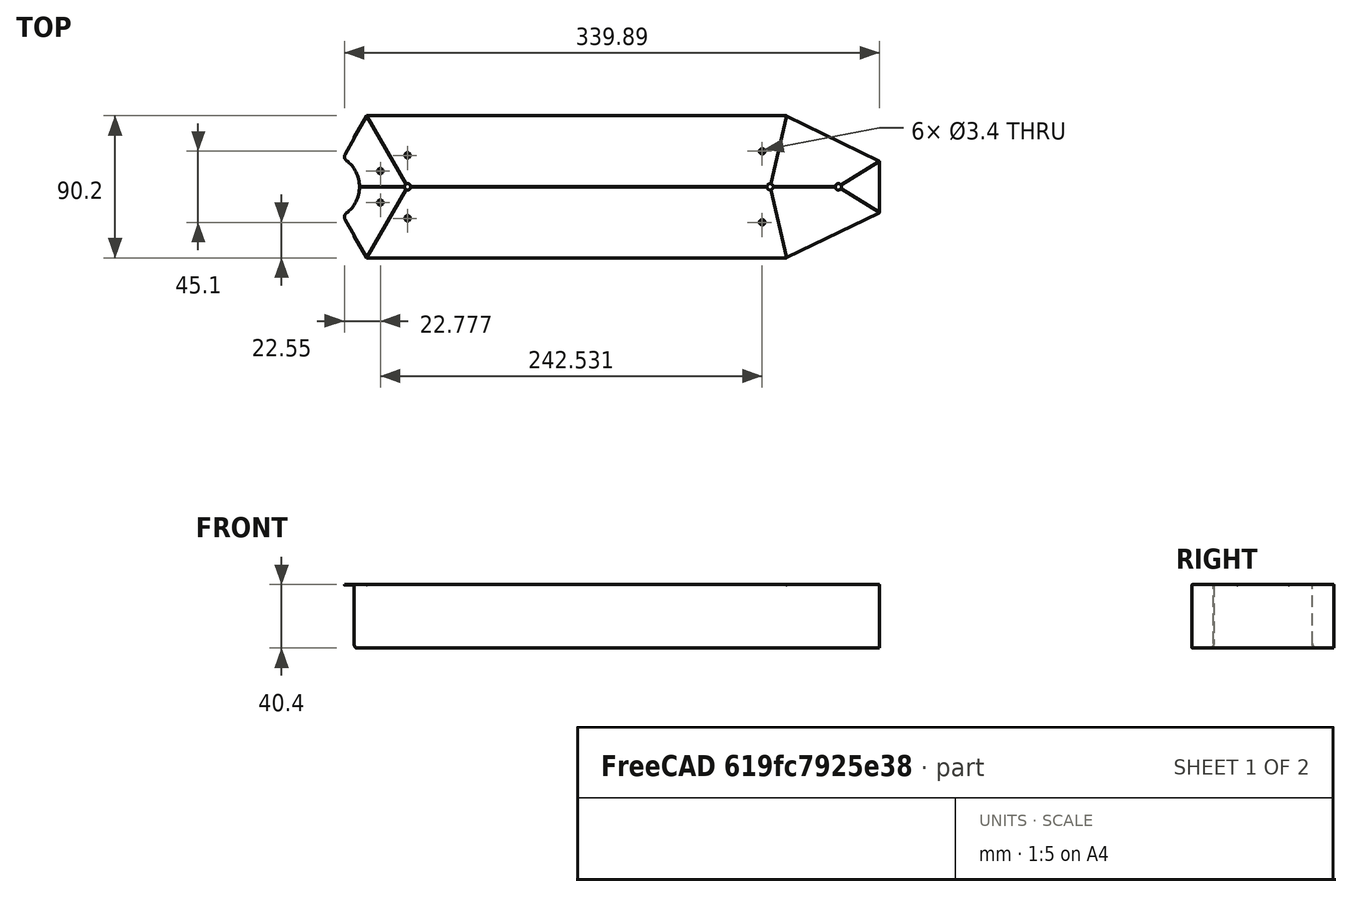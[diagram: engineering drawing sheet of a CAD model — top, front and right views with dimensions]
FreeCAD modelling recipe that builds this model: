
FCSTD DOCUMENT  (FreeCAD 1.1R38827 (Git))
Label: composit_stand3_dropper_fix_cap_outer_main
License: All rights reserved
LicenseURL: http://en.wikipedia.org/wiki/All_rights_reserved
objects: Part::FeaturePython×8, Sketcher::SketchObject×4, Part::Feature×1, PartDesign::SubShapeBinder×1, Part::Offset2D×1, Spreadsheet::Sheet×1
note: 19 computed .brp shape members not serialized (recipe doc carries the construction recipe); baked Part::Feature solids carry a one-line shape summary decoded from their .brp
EXTERNAL_REF file=composit_stand3_dropper_fix_main.FCStd obj=Sketch

FEATURE [Part::Feature] Body168  label="cap_outer_material_0.30ansi002"
  Placement = pos=(0,0,0) rot=(0,0,-1;1.5708rad)
  shape: bbox 339.9 x 90.2 x 40.4 mm, 133 faces (baked)
FEATURE [PartDesign::SubShapeBinder] Binder
  BindCopyOnChange = 0
  BindMode = 0
  ClaimChildren = false
  Fuse = false
  MakeFace = true
  OffsetFill = false
  OffsetIntersection = false
  OffsetJoinType = 0
  OffsetOpenResult = false
  PartialLoad = false
  Relative = true
  Support = -> [<external composit_stand3_dropper_fix_main.FCStd>#Sketch]
  _Version = 2
FEATURE [Sketcher::SketchObject] Sketch  label="main_sketch"
  ArcFitTolerance = 0
  ExternalGeometry = -> [Binder]
  FullyConstrained = true
  MakeInternals = false
  sketch-geometry (10):
    g0: LineSegment StartX=351.872 StartY=0 StartZ=0 EndX=351.872 EndY=16.378 EndZ=0
    g1: LineSegment StartX=351.872 StartY=16.378 StartZ=0 EndX=292.736 EndY=45.1 EndZ=0
    g2: LineSegment StartX=292.736 StartY=45.1 StartZ=0 EndX=26.0385 EndY=45.1 EndZ=0
    g3: LineSegment StartX=26.0385 StartY=45.1 StartZ=0 EndX=0.23094 EndY=0.4 EndZ=0
    g4: LineSegment [constr] StartX=292.046 StartY=45.1 StartZ=0 EndX=292.046 EndY=42.1 EndZ=0
    g5: LineSegment [constr] StartX=292.046 StartY=42.1 StartZ=0 EndX=293.356 EndY=44.7985 EndZ=0
    g6: LineSegment [constr] StartX=351.872 StartY=14.5 StartZ=0 EndX=348.872 EndY=14.5 EndZ=0
    g7: LineSegment [constr] StartX=348.872 StartY=14.5 StartZ=0 EndX=350.182 EndY=17.1985 EndZ=0
    g8: LineSegment [constr] StartX=27.7705 StartY=45.1 StartZ=0 EndX=27.7705 EndY=42.1 EndZ=0
    g9: LineSegment [constr] StartX=27.7705 StartY=42.1 StartZ=0 EndX=25.1725 EndY=43.6 EndZ=0
  constraints (31):
    c: Vertical(g0)
    c: Coincident(g0,g1)
    c: Coincident(g1,g2)
    c: Horizontal(g2)
    c: Coincident(g2,g3)
    c: PointOnObject(g0,g-1)
    c: PointOnObject(g4,g2)
    c: Coincident(g4,g-4)
    c: Vertical(g4)
    c: Coincident(g4,g5)
    c: PointOnObject(g5,g1)
    c: PointOnObject(g6,g0)
    c: Coincident(g6,g-3)
    c: Horizontal(g6)
    c: Coincident(g6,g7)
    c: PointOnObject(g7,g1)
    c: Perpendicular(g1,g7)
    c: Perpendicular(g1,g5)
    c: Equal(g6,g7)
    c: Equal(g7,g5)
    c: DistanceX(g-3,g0) = 3
    c: Equal(g4,g5)
    c: PointOnObject(g8,g2)
    c: Coincident(g8,g-5)
    c: Vertical(g8)
    c: Coincident(g8,g9)
    c: PointOnObject(g9,g3)
    c: Perpendicular(g3,g9)
    c: Equal(g9,g8)
    c: Parallel(g3,g-5)
    c: DistanceY(g3) = 0.4
FEATURE [Part::Offset2D] Offset2D
  Fill = false
  Intersection = false
  Join = 0
  Mode = 0
  SelfIntersection = false
  Source = -> Sketch
  Value = -0.4
FEATURE [Sketcher::SketchObject] Sketch001
  ArcFitTolerance = 0
  ExternalGeometry = -> [Offset2D]
  FullyConstrained = true
  MakeInternals = false
  sketch-geometry (11):
    g0: LineSegment StartX=351.472 StartY=16.1276 StartZ=0 EndX=325.709 EndY=0 EndZ=0
    g1: LineSegment [constr] StartX=336.965 StartY=23.1736 StartZ=0 EndX=325.709 EndY=0 EndZ=0
    g2: LineSegment [constr] StartX=325.709 StartY=0 StartZ=0 EndX=351.472 EndY=0 EndZ=0
    g3: LineSegment StartX=292.644 StartY=44.7 StartZ=0 EndX=282.363 EndY=0 EndZ=0
    g4: LineSegment [constr] StartX=301.892 StartY=40.2083 StartZ=0 EndX=282.363 EndY=0 EndZ=0
    g5: LineSegment [constr] StartX=282.363 StartY=0 StartZ=0 EndX=282.363 EndY=44.7 EndZ=0
    g6: LineSegment StartX=325.709 StartY=0 StartZ=0 EndX=282.363 EndY=0 EndZ=0
    g7: LineSegment StartX=282.363 StartY=0 StartZ=0 EndX=52.077 EndY=0 EndZ=0
    g8: LineSegment StartX=52.077 StartY=0 StartZ=0 EndX=26.2694 EndY=44.7 EndZ=0
    g9: LineSegment [constr] StartX=52.077 StartY=44.7 StartZ=0 EndX=52.077 EndY=0 EndZ=0
    g10: LineSegment [constr] StartX=52.077 StartY=0 StartZ=0 EndX=13.3657 EndY=22.35 EndZ=0
  constraints (31):
    c: Coincident(g1,g2)
    c: Horizontal(g2)
    c: Vertical(g2,g0)
    c: Equal(g1,g2)
    c: Coincident(g1,g0)
    c: PointOnObject(g0,g-1)
    c: PointOnObject(g3,g-1)
    c: Coincident(g4,g3)
    c: Coincident(g4,g5)
    c: Vertical(g5)
    c: Horizontal(g5,g3)
    c: Equal(g4,g5)
    c: Coincident(g0,g6)
    c: Coincident(g6,g3)
    c: Coincident(g6,g7)
    c: PointOnObject(g7,g-1)
    c: Coincident(g7,g8)
    c: Coincident(g9,g7)
    c: Vertical(g9)
    c: Coincident(g9,g10)
    c: Horizontal(g9,g8)
    c: Equal(g10,g9)
    c: Coincident(g0,g-4)
    c: PointOnObject(g1,g-4)
    c: Perpendicular(g-4,g1)
    c: Coincident(g3,g-4)
    c: PointOnObject(g4,g-4)
    c: Perpendicular(g-4,g4)
    c: PointOnObject(g10,g-3)
    c: Perpendicular(g-3,g10)
    c: Coincident(g8,g-3)
FEATURE [Sketcher::SketchObject] Sketch002  label="top_cut_sketch"
  ArcFitTolerance = 0
  ExternalGeometry = -> [Sketch001,Sketch,Offset2D]
  FullyConstrained = true
  MakeInternals = false
  sketch-geometry (34):
    g0: LineSegment StartX=26.3272 StartY=44.7 StartZ=0 EndX=52.1059 EndY=0.05 EndZ=0
    g1: LineSegment StartX=52.1059 StartY=0.05 StartZ=0 EndX=282.323 EndY=0.05 EndZ=0
    g2: LineSegment StartX=282.323 StartY=0.05 StartZ=0 EndX=292.592 EndY=44.7 EndZ=0
    g3: LineSegment StartX=292.69 StartY=44.6776 StartZ=0 EndX=282.425 EndY=0.05 EndZ=0
    g4: LineSegment StartX=282.425 StartY=0.05 StartZ=0 EndX=325.695 EndY=0.05 EndZ=0
    g5: LineSegment StartX=325.695 StartY=0.05 StartZ=0 EndX=351.419 EndY=16.1534 EndZ=0
    g6: LineSegment StartX=351.472 StartY=16.0687 StartZ=0 EndX=325.803 EndY=0 EndZ=0
    g7: LineSegment [constr] StartX=51.9904 StartY=0.05 StartZ=0 EndX=52.1059 EndY=0.05 EndZ=0
    g8: LineSegment [constr] StartX=282.323 StartY=0.05 StartZ=0 EndX=282.425 EndY=0.05 EndZ=0
    g9: LineSegment [constr] StartX=325.695 StartY=0.05 StartZ=0 EndX=325.883 EndY=0.05 EndZ=0
    g10: LineSegment [constr] StartX=51.9904 StartY=0 StartZ=0 EndX=51.9904 EndY=0.05 EndZ=0
    g11: LineSegment [constr] StartX=51.9904 StartY=0.05 StartZ=0 EndX=52.0337 EndY=0.075 EndZ=0
    g12: LineSegment [constr] StartX=52.0337 StartY=0.075 StartZ=0 EndX=52.077 EndY=0.1 EndZ=0
    g13: LineSegment [constr] StartX=282.425 StartY=0.05 StartZ=0 EndX=282.377 EndY=0.0612074 EndZ=0
    g14: LineSegment [constr] StartX=282.377 StartY=0.0612074 StartZ=0 EndX=282.328 EndY=0.0724148 EndZ=0
    g15: LineSegment [constr] StartX=325.883 StartY=0.05 StartZ=0 EndX=325.857 EndY=0.0923805 EndZ=0
    g16: LineSegment [constr] StartX=325.857 StartY=0.0923805 StartZ=0 EndX=325.83 EndY=0.134761 EndZ=0
    g17: LineSegment StartX=351.419 StartY=16.1534 StartZ=0 EndX=351.593 EndY=16.5132 EndZ=0
    g18: LineSegment StartX=351.593 StartY=16.5132 StartZ=0 EndX=351.872 EndY=16.378 EndZ=0
    g19: LineSegment StartX=351.872 StartY=16.378 StartZ=0 EndX=351.872 EndY=16.0687 EndZ=0
    g20: LineSegment StartX=351.872 StartY=16.0687 StartZ=0 EndX=351.472 EndY=16.0687 EndZ=0
    g21: LineSegment [constr] StartX=351.419 StartY=16.1534 StartZ=0 EndX=351.472 EndY=16.1276 EndZ=0
    g22: LineSegment [constr] StartX=351.472 StartY=16.1276 StartZ=0 EndX=351.472 EndY=16.0687 EndZ=0
    g23: LineSegment StartX=26.2406 StartY=44.65 StartZ=0 EndX=25.8942 EndY=44.85 EndZ=0
    g24: LineSegment StartX=25.8942 StartY=44.85 StartZ=0 EndX=26.0385 EndY=45.1 EndZ=0
    g25: LineSegment StartX=26.0385 StartY=45.1 StartZ=0 EndX=26.3272 EndY=45.1 EndZ=0
    g26: LineSegment StartX=26.3272 StartY=45.1 StartZ=0 EndX=26.3272 EndY=44.7 EndZ=0
    g27: LineSegment StartX=292.592 StartY=44.7 StartZ=0 EndX=292.592 EndY=45.1 EndZ=0
    g28: LineSegment StartX=292.592 StartY=45.1 StartZ=0 EndX=292.736 EndY=45.1 EndZ=0
    g29: LineSegment StartX=292.736 StartY=45.1 StartZ=0 EndX=292.864 EndY=45.0374 EndZ=0
    g30: LineSegment StartX=292.864 StartY=45.0374 StartZ=0 EndX=292.69 EndY=44.6776 EndZ=0
    g31: LineSegment StartX=26.2406 StartY=44.65 StartZ=0 EndX=51.9904 EndY=0.05 EndZ=0
    g32: LineSegment StartX=51.9904 StartY=0.05 StartZ=0 EndX=0 EndY=0.05 EndZ=0
    g33: LineSegment StartX=0 StartY=0.05 StartZ=0 EndX=0 EndY=0 EndZ=0
  constraints (95):
    c: Coincident(g0,g1)
    c: Horizontal(g1)
    c: Coincident(g1,g2)
    c: Coincident(g3,g4)
    c: Horizontal(g4)
    c: Coincident(g4,g5)
    c: Coincident(g7,g0)
    c: Horizontal(g7)
    c: Coincident(g8,g1)
    c: Coincident(g8,g3)
    c: Horizontal(g8)
    c: Coincident(g9,g4)
    c: Horizontal(g9)
    c: Parallel(g6,g-4)
    c: Parallel(g-4,g5)
    c: Parallel(g3,g-3)
    c: Parallel(g-3,g2)
    c: Parallel(g0,g-5)
    c: PointOnObject(g10,g-1)
    c: Coincident(g10,g11)
    c: PointOnObject(g11,g-5)
    c: Coincident(g11,g12)
    c: PointOnObject(g12,g0)
    c: Vertical(g10)
    c: Equal(g10,g11)
    c: Equal(g11,g12)
    c: Coincident(g3,g13)
    c: PointOnObject(g13,g-3)
    c: Coincident(g13,g14)
    c: PointOnObject(g14,g2)
    c: PointOnObject(g15,g-4)
    c: Coincident(g15,g16)
    c: PointOnObject(g16,g5)
    c: Equal(g15,g16)
    c: Equal(g16,g13)
    c: Equal(g13,g14)
    c: Equal(g14,g12)
    c: Perpendicular(g-5,g11)
    c: Perpendicular(g12,g-5)
    c: Perpendicular(g13,g-3)
    c: Perpendicular(g14,g-3)
    c: Perpendicular(g15,g-4)
    c: Perpendicular(g16,g-4)
    c: Coincident(g5,g17)
    c: PointOnObject(g17,g-6)
    c: Coincident(g17,g18)
    c: Coincident(g18,g-6)
    c: Coincident(g18,g19)
    c: Vertical(g19)
    c: Coincident(g19,g20)
    c: Coincident(g20,g6)
    c: Horizontal(g20)
    c: Coincident(g5,g21)
    c: Coincident(g21,g-4)
    c: Coincident(g21,g22)
    c: Coincident(g22,g6)
    c: Vertical(g22)
    c: PointOnObject(g5,g-7)
    c: Perpendicular(g17,g21)
    c: DistanceY(g10,g10) = 0.05
    c: Coincident(g31,g23)
    c: Coincident(g23,g24)
    c: Coincident(g24,g25)
    c: Horizontal(g25)
    c: Coincident(g25,g26)
    c: Coincident(g26,g0)
    c: Vertical(g26)
    c: Coincident(g24,g-8)
    c: Perpendicular(g24,g23)
    c: Equal(g26,g23)
    c: Equal(g23,g20)
    c: Equal(g25,g24)
    c: Coincident(g2,g27)
    c: Vertical(g27)
    c: Coincident(g27,g28)
    c: Coincident(g28,g-6)
    c: Coincident(g28,g29)
    c: PointOnObject(g29,g-6)
    c: Coincident(g29,g30)
    c: Coincident(g30,g3)
    c: Horizontal(g28)
    c: Perpendicular(g29,g30)
    c: Equal(g30,g27)
    c: Equal(g30,g17)
    c: Coincident(g7,g10)
    c: PointOnObject(g9,g6)
    c: Coincident(g9,g15)
    c: PointOnObject(g6,g-1)
    c: Parallel(g-5,g31)
    c: Coincident(g31,g7)
    c: Coincident(g7,g32)
    c: Horizontal(g32)
    c: Coincident(g33,g32)
    c: Coincident(g33,g-1)
    c: Vertical(g33)
FEATURE [Part::FeaturePython] Placment  # WARN: FeaturePython — macro-defined, semantics opaque (R4)
  AttacherType = Attacher::AttachEngine3D
  AttachmentSupport = -> [Sketch001]
  ExposePlacement = true
  MapMode = 1
  MarkerShape = 1
  MarkerSize = 10
  NumElements = 1
  Placement = pos=(52.077,0,0) rot=(0,0,1;0rad)
  Type = lattice2AttachablePlacement.AttachablePlacement
  isLattice = 1
FEATURE [Part::FeaturePython] Placment001  # WARN: FeaturePython — macro-defined, semantics opaque (R4)
  AttacherType = Attacher::AttachEngine3D
  AttachmentSupport = -> [Sketch001]
  ExposePlacement = true
  MapMode = 1
  MarkerShape = 1
  MarkerSize = 10
  NumElements = 1
  Placement = pos=(282.363,0,0) rot=(0,0,1;0rad)
  Type = lattice2AttachablePlacement.AttachablePlacement
  isLattice = 1
FEATURE [Part::FeaturePython] Placment002  # WARN: FeaturePython — macro-defined, semantics opaque (R4)
  AttacherType = Attacher::AttachEngine3D
  AttachmentSupport = -> [Sketch001]
  ExposePlacement = true
  MapMode = 1
  MarkerShape = 1
  MarkerSize = 10
  NumElements = 1
  Placement = pos=(325.709,0,0) rot=(0,0,1;0rad)
  Type = lattice2AttachablePlacement.AttachablePlacement
  isLattice = 1
FEATURE [Sketcher::SketchObject] Sketch003
  ArcFitTolerance = 0
  ExternalGeometry = -> [Sketch001]
  FullyConstrained = true
  MakeInternals = false
  sketch-geometry (9):
    g0: Circle CenterX=34.7565 CenterY=10 CenterZ=0 NormalX=0 NormalY=0 NormalZ=1 AngleXU=0 Radius=1.7
    g1: Circle CenterX=52.077 CenterY=20 CenterZ=0 NormalX=0 NormalY=0 NormalZ=1 AngleXU=0 Radius=1.7
    g2: Circle CenterX=276.702 CenterY=20 CenterZ=0 NormalX=0 NormalY=0 NormalZ=1 AngleXU=0 Radius=1.7
    g3: LineSegment [constr] StartX=52.077 StartY=0 StartZ=0 EndX=52.077 EndY=20 EndZ=0
    g4: LineSegment [constr] StartX=34.7565 StartY=10 StartZ=0 EndX=34.7565 EndY=0 EndZ=0
    g5: LineSegment [constr] StartX=52.077 StartY=20 StartZ=0 EndX=43.4167 EndY=15 EndZ=0
    g6: LineSegment [constr] StartX=43.4167 StartY=15 StartZ=0 EndX=34.7565 EndY=10 EndZ=0
    g7: LineSegment [constr] StartX=52.077 StartY=20 StartZ=0 EndX=276.702 EndY=20 EndZ=0
    g8: LineSegment [constr] StartX=276.702 StartY=20 StartZ=0 EndX=286.447 EndY=17.7585 EndZ=0
  constraints (24):
    c: Coincident(g3,g1)
    c: Vertical(g3)
    c: Coincident(g3,g5)
    c: Coincident(g6,g0)
    c: Coincident(g6,g4)
    c: PointOnObject(g4,g-1)
    c: Vertical(g4)
    c: Coincident(g5,g6)
    c: Parallel(g5,g6)
    c: Diameter(g1) = 3.4
    c: Equal(g1,g0)
    c: Equal(g2,g1)
    c: Equal(g5,g6)
    c: Coincident(g7,g1)
    c: Coincident(g7,g2)
    c: Distance(g5) = 10
    c: PointOnObject(g5,g-3)
    c: Coincident(g3,g-3)
    c: Perpendicular(g-3,g5)
    c: Coincident(g8,g2)
    c: PointOnObject(g8,g-4)
    c: Perpendicular(g-4,g8)
    c: Equal(g8,g5)
    c: Horizontal(g7)
FEATURE [Part::FeaturePython] Downgrade  label="Edges of Sketch003"  # WARN: FeaturePython — macro-defined, semantics opaque (R4)
  Base = -> Sketch003
  Mode = 8
FEATURE [Part::FeaturePython] ArrayFromShape  label="Array from Edges of Sketch003"  # WARN: FeaturePython — macro-defined, semantics opaque (R4)
  CompoundTraversal = 1
  ExposePlacement = false
  MarkerShape = 1
  MarkerSize = 50
  NumElements = 3
  OrientElementIndex = 0
  OrientMode = 2
  ShapeLink = -> Downgrade
  TranslateElementIndex = 0
  TranslateMode = 3
  Type = lattice2ArrayFromShape.LatticeArrayFromShape
  isLattice = 1
FEATURE [Part::FeaturePython] Mirror  label="Mirror of Array from Edges of Sketch003"  # WARN: FeaturePython — macro-defined, semantics opaque (R4)
  ExposePlacement = false
  FlipX = false
  FlipY = true
  FlipZ = false
  MarkerShape = 1
  MarkerSize = 0
  NumElements = 3
  Object = -> ArrayFromShape
  ObjectTraversal = 0
  Type = lattice2Mirror.LatticeMirror
  isLattice = 1
FEATURE [Part::FeaturePython] Join  label="holes_3.4mm_placements"  # WARN: FeaturePython — macro-defined, semantics opaque (R4)
  ExposePlacement = false
  Interleave = false
  Links = -> [ArrayFromShape,Mirror]
  MarkerShape = 1
  MarkerSize = 0
  NumElements = 6
  Placement = pos=(0,0,40) rot=(0,0,1;0rad)
  Type = lattice2JoinArrays.JoinArrays
  isLattice = 1
  expr: .Placement.Base.z = <<Properties>>.height
FEATURE [Part::FeaturePython] Join001  label="holes_4mm_placements"  # WARN: FeaturePython — macro-defined, semantics opaque (R4)
  ExposePlacement = false
  Interleave = false
  Links = -> [Placment,Placment002,Placment001]
  MarkerShape = 1
  MarkerSize = 0
  NumElements = 3
  Placement = pos=(0,0,40) rot=(0,0,1;0rad)
  Type = lattice2JoinArrays.JoinArrays
  isLattice = 1
  expr: .Placement.Base.z = <<Properties>>.height
FEATURE [Spreadsheet::Sheet] Spreadsheet  label="Properties"
  cells = B2(height)==40 mm; C2(width)=
